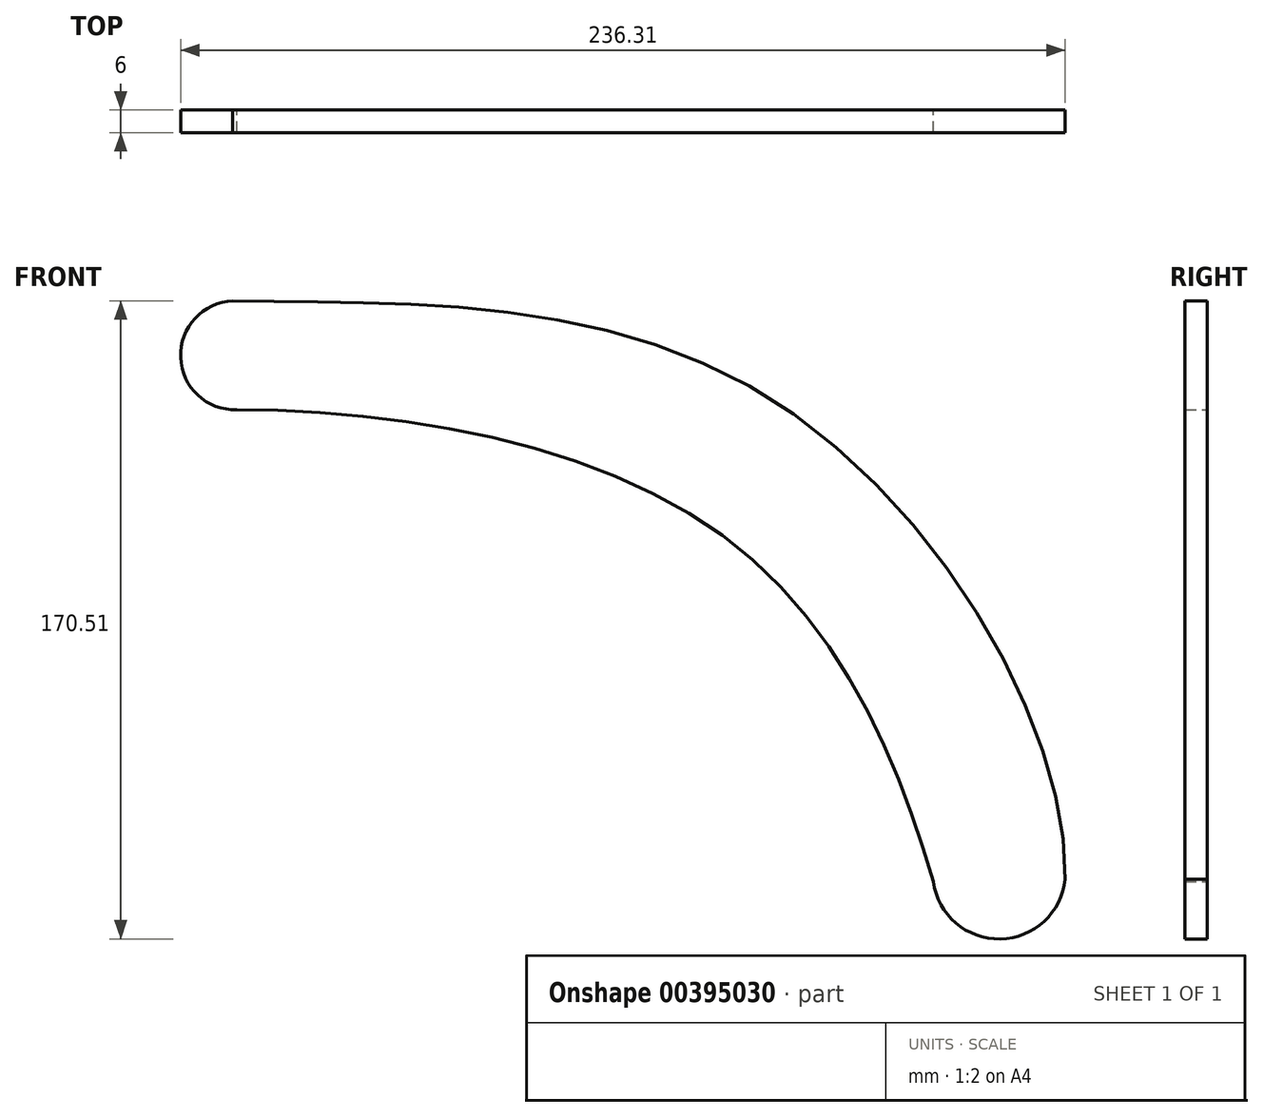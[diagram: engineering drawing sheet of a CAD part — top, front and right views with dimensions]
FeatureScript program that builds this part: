
annotation { "Feature Type Name" : "Feature", "Feature Type Description" : "" }
export const myFeature = defineFeature(function(context is Context, id is Id, definition is map)
    precondition{}
    {
        {
            var Q0;
            Q0=qCreatedBy(makeId("Front.planeOp"),FACE);
            var sketch = newSketch(context, id + "F0", { "sketchPlane" : qUnion([Q0])});
            skFitSpline(sketch, "E0", {"points": [v(-101.71, 76.8) * mm, v(40.48, 51.57) * mm, v(120.6, -77.7) * mm], "startDerivative": vector(245.5, -4.94) * mm, "endDerivative": vector(-5.96, -237.41) * mm});
            skFitSpline(sketch, "E1", {"points": [v(-100.64, 47.72) * mm, v(30.8, 12.82) * mm, v(85.38, -78.39) * mm], "startDerivative": vector(248.36, 0) * mm, "endDerivative": vector(58.6, -204.02) * mm});
            skArc(sketch, "E2", {"start": v(-101.71, 76.8) * mm, "mid": v(-115.67, 61.72) * mm, "end": v(-100.64, 47.72) * mm});
            skArc(sketch, "E3", {"start": v(85.38, -78.39) * mm, "mid": v(103.3, -93.71) * mm, "end": v(120.6, -77.7) * mm});
            skSolve(sketch);
        }
        {
            var Q0;
            Q0=makeQuery(id+"F0.imprint","IMPRINT",FACE,{"disambiguationData":[TD([[makeQuery(id+"F0.imprint","IMPRINT",EDGE,{"derivedFrom":sQuery(id+"F0.wireOp",EDGE,"E0")}),-1.0]])]});
            extrude(context, id + "F1", {"entities" : qUnion([Q0]), "depth" : 6 * mm});
        }
    });
